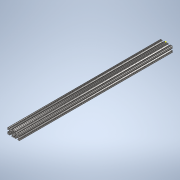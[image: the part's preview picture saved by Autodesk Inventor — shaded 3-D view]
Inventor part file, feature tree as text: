
AUTODESK INVENTOR PART (.ipt)
format: ipt  version: 2020 (Build 240168000, 168)  size: 356,864 bytes
history: native  units: in
note: dims shown in document units (in); Inventor stores cm internally (conversion verified against a paired STEP export)
features: sketch x2, extrude x1
ambient origin geometry x8: Origin, YZ Plane, XZ Plane, XY Plane, X Axis, Y Axis, Z Axis, Center Point
bodies: Solid1 (feature_tree)
feature tree (3):
  extrude  "Extrusion1"  [1 undecoded]
  sketch  "Sketch2"
  sketch  "Sketch1"  dims[d0=25.0in d1=0.0in]
note: 1 required parameter value undecoded (feature->parameter linkage not recoverable at this tier; creation-order binding heuristic only, values carry confidence <= 0.55)
